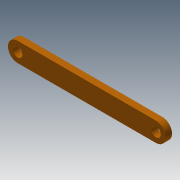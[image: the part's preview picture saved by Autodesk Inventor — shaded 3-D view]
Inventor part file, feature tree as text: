
AUTODESK INVENTOR PART (.ipt)
format: ipt  version: 2013 (Build 170138000, 138)  size: 106,496 bytes
history: native  units: mm
features: extrude x4, sketch x4
ambient origin geometry x8: Origin, YZ Plane, XZ Plane, XY Plane, X Axis, Y Axis, Z Axis, Center Point
bodies: Solid1 (feature_tree)
feature tree (8):
  extrude  "Extrusion1"  Depth=6.0mm
  extrude  "Extrusion2"  Depth=3.0mm
  extrude  "Extrusion3"  Depth=2.0mm TaperAngle=0.0deg
  extrude  "Extrusion4"  Depth=0.1mm
  sketch  "Sketch1"  dims[d0=43.0mm d1=6.0mm]
  sketch  "Sketch2"  dims[d3=2.0mm d4=0.0mm d5=3.0mm]
  sketch  "Sketch3"  dims[d6=3.0mm d7=2.0mm d8=0.0mm]
  sketch  "Sketch4"  dims[d9=0.1mm d10=0.1mm d11=2.0mm d12=0.0mm d13=3.0mm d14=3.0mm d15=2.0mm d16=0.0mm]
